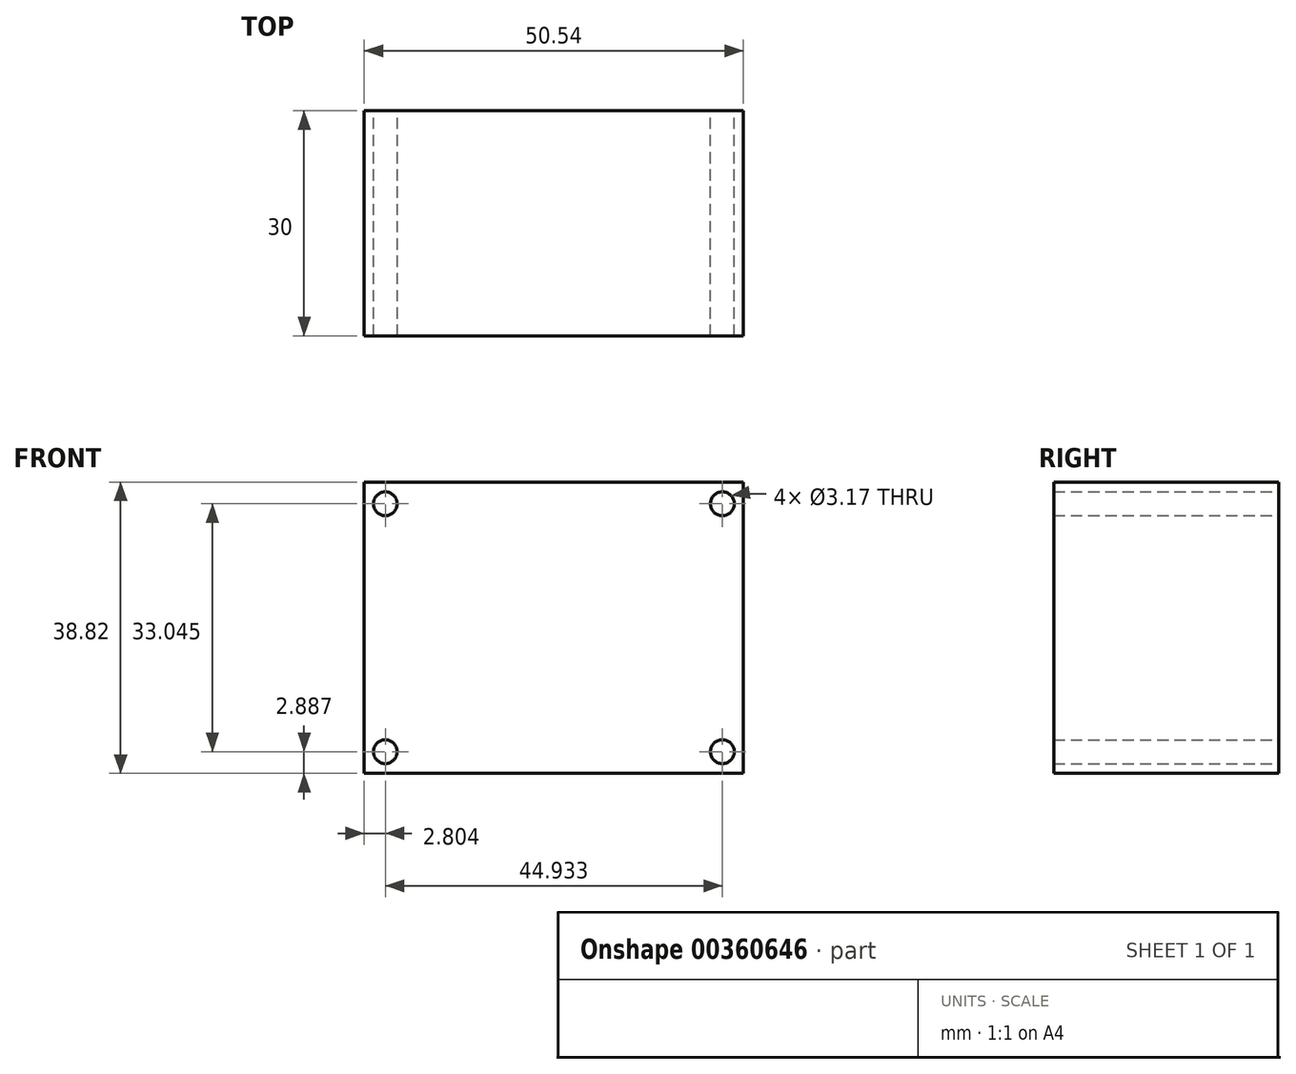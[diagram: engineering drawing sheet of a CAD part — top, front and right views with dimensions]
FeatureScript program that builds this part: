
annotation { "Feature Type Name" : "Feature", "Feature Type Description" : "" }
export const myFeature = defineFeature(function(context is Context, id is Id, definition is map)
    precondition{}
    {
        {
            var Q0;
            Q0=qCreatedBy(makeId("Front.planeOp"),FACE);
            var sketch = newSketch(context, id + "F0", { "sketchPlane" : qUnion([Q0])});
            skLineSegment(sketch, "E0.bottom", {"start": v(-25.27, 19.41) * mm, "end": v(25.27, 19.41) * mm});
            skLineSegment(sketch, "E0.top", {"start": v(-25.27, -19.41) * mm, "end": v(25.27, -19.41) * mm});
            skLineSegment(sketch, "E0.left", {"start": v(-25.27, 19.41) * mm, "end": v(-25.27, -19.41) * mm});
            skLineSegment(sketch, "E0.right", {"start": v(25.27, 19.41) * mm, "end": v(25.27, -19.41) * mm});
            skPoint(sketch, "E1", {"position": v(0, 19.41) * mm});
            skPoint(sketch, "E2", {"position": v(25.27, 0) * mm});
            skLineSegment(sketch, "E3.bottom", {"start": v(-22.47, 16.52) * mm, "end": v(22.47, 16.52) * mm, "construction": true});
            skLineSegment(sketch, "E3.top", {"start": v(-22.47, -16.52) * mm, "end": v(22.47, -16.52) * mm, "construction": true});
            skLineSegment(sketch, "E3.left", {"start": v(-22.47, 16.52) * mm, "end": v(-22.47, -16.52) * mm, "construction": true});
            skLineSegment(sketch, "E3.right", {"start": v(22.47, 16.52) * mm, "end": v(22.47, -16.52) * mm, "construction": true});
            skPoint(sketch, "E4", {"position": v(0, 16.52) * mm});
            skPoint(sketch, "E5", {"position": v(22.47, 0) * mm});
            skCircle(sketch, "E6", {"center": v(-22.47, 16.52) * mm, "radius": 1.59 * mm});
            skCircle(sketch, "E7", {"center": v(-22.47, -16.52) * mm, "radius": 1.59 * mm});
            skCircle(sketch, "E8", {"center": v(22.47, -16.52) * mm, "radius": 1.59 * mm});
            skCircle(sketch, "E9", {"center": v(22.47, 16.52) * mm, "radius": 1.59 * mm});
            skSolve(sketch);
        }
        {
            var Q0;
            Q0 = qSketchRegion(id + "F0", true);
            extrude(context, id + "F1", {"entities" : qUnion([Q0]), "depth" : 30 * mm});
        }
    });
